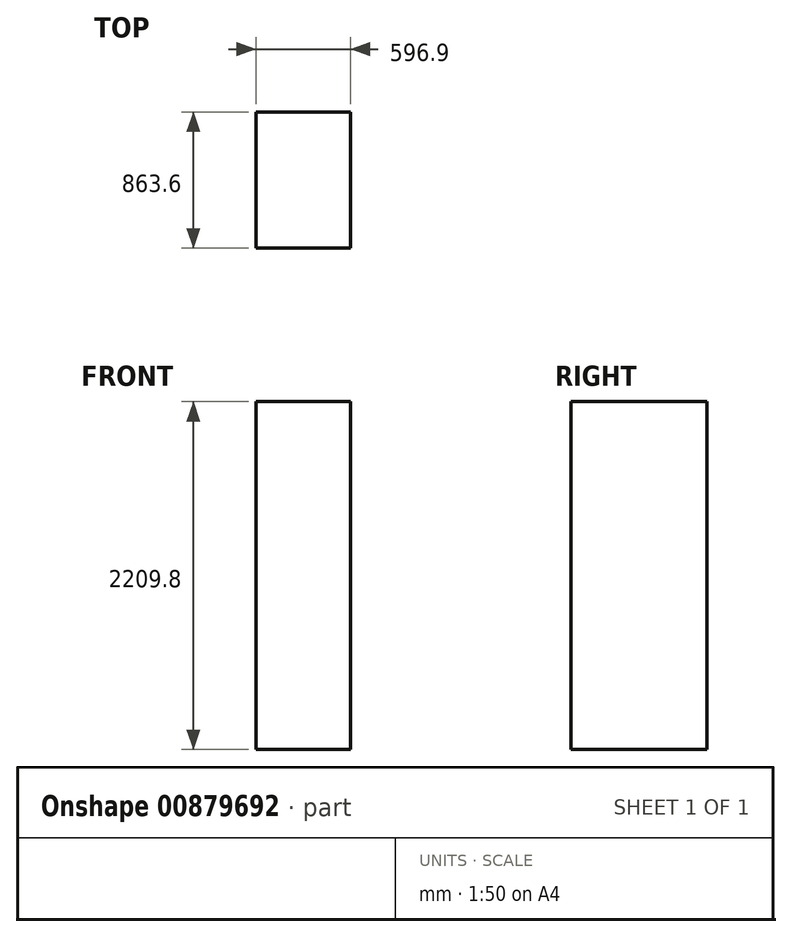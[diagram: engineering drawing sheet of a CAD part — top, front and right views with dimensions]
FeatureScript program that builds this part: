
annotation { "Feature Type Name" : "Feature", "Feature Type Description" : "" }
export const myFeature = defineFeature(function(context is Context, id is Id, definition is map)
    precondition{}
    {
        {
            var Q0;
            Q0=qCreatedBy(makeId("Top.planeOp"),FACE);
            var sketch = newSketch(context, id + "F0", { "sketchPlane" : qUnion([Q0])});
            skLineSegment(sketch, "E0.bottom", {"start": v(-410.78, 83.17) * mm, "end": v(186.12, 83.17) * mm});
            skLineSegment(sketch, "E0.top", {"start": v(-410.78, -780.43) * mm, "end": v(186.12, -780.43) * mm});
            skLineSegment(sketch, "E0.left", {"start": v(-410.78, 83.17) * mm, "end": v(-410.78, -780.43) * mm});
            skLineSegment(sketch, "E0.right", {"start": v(186.12, 83.17) * mm, "end": v(186.12, -780.43) * mm});
            skSolve(sketch);
        }
        {
            var Q0;
            Q0=makeQuery(id+"F0.imprint","IMPRINT",FACE,{"disambiguationData":[TD([[makeQuery(id+"F0.imprint","IMPRINT",EDGE,{"derivedFrom":sQuery(id+"F0.wireOp",EDGE,"E0.bottom")}),-1.0]])]});
            extrude(context, id + "F1", {"entities" : qUnion([Q0]), "depth" : 2209.8 * mm, "offsetDistance" : 25.4 * mm});
        }
    });
